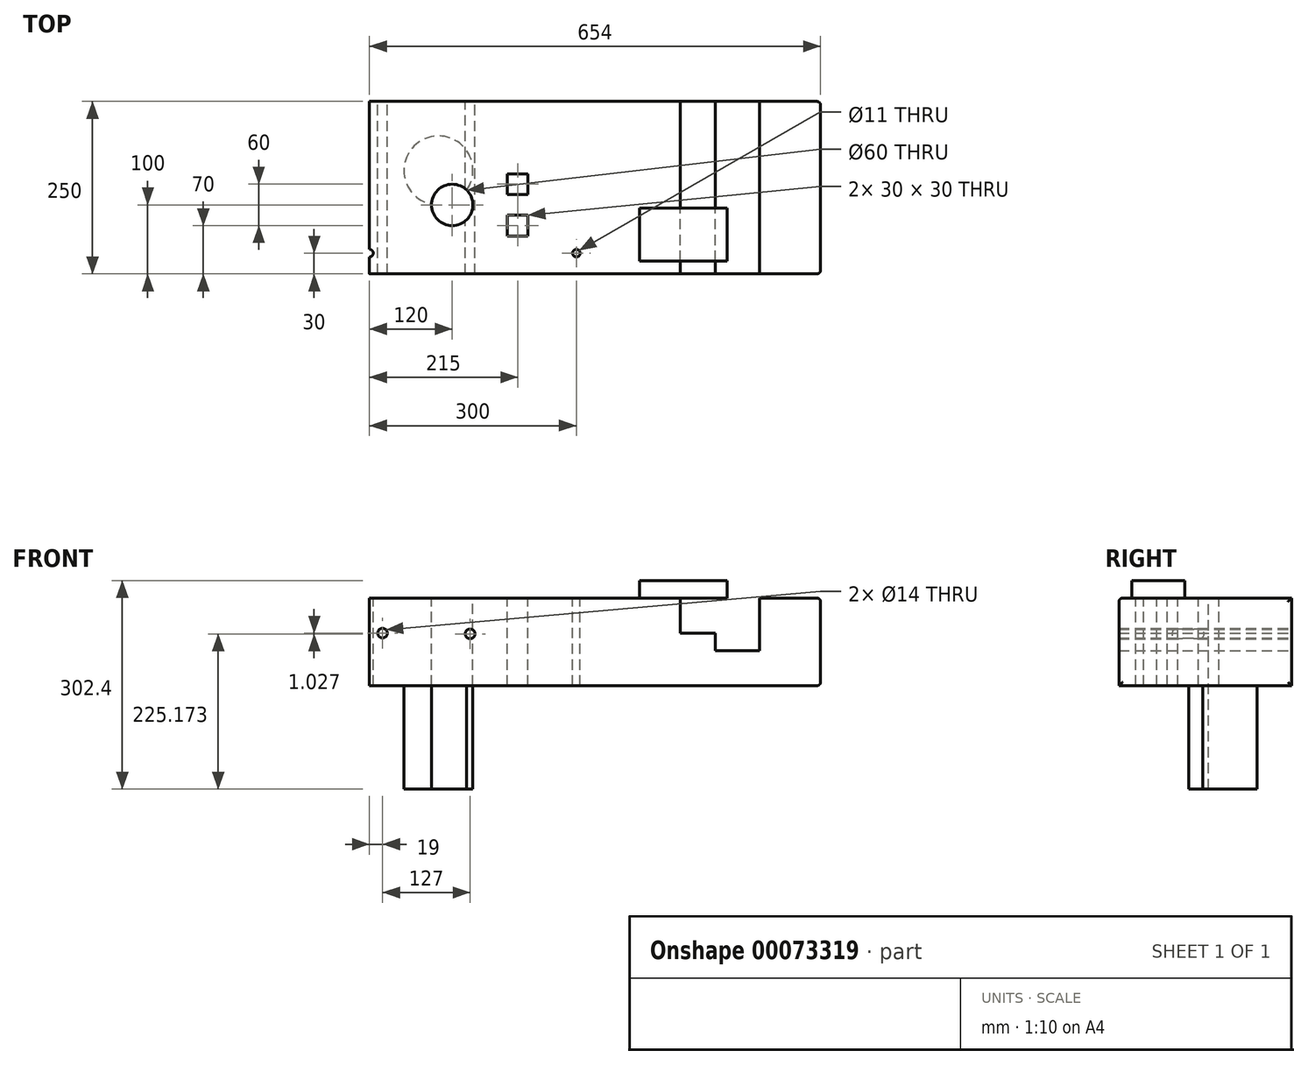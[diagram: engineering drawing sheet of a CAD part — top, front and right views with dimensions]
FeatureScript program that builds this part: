
annotation { "Feature Type Name" : "Feature", "Feature Type Description" : "" }
export const myFeature = defineFeature(function(context is Context, id is Id, definition is map)
    precondition{}
    {
        {
            var Q0;
            Q0=qCreatedBy(makeId("Top.planeOp"),FACE);
            var sketch = newSketch(context, id + "F0", { "sketchPlane" : qUnion([Q0])});
            skLineSegment(sketch, "E0.bottom", {"start": v(0, 0) * mm, "end": v(-400, 0) * mm});
            skLineSegment(sketch, "E0.top", {"start": v(0, -250) * mm, "end": v(-400, -250) * mm});
            skLineSegment(sketch, "E0.left", {"start": v(0, 0) * mm, "end": v(0, -250) * mm});
            skLineSegment(sketch, "E0.right", {"start": v(-400, 0) * mm, "end": v(-400, -250) * mm});
            skSolve(sketch);
        }
        {
            var Q0;
            Q0 = qSketchRegion(id + "F0", true);
            extrude(context, id + "F1", {"entities" : qUnion([Q0]), "depth" : 127 * mm});
        }
        {
            var Q0;
            Q0=makeQuery(id+"F1.opExtrude","CAP_FACE",FACE,{"disambiguationData":[OSD([sQuery(id+"F0.wireOp",EDGE,"E0.bottom"),sQuery(id+"F0.wireOp",EDGE,"E0.top"),sQuery(id+"F0.wireOp",EDGE,"E0.left"),sQuery(id+"F0.wireOp",EDGE,"E0.right")])],"isStart":true});
            var sketch = newSketch(context, id + "F2", { "sketchPlane" : qUnion([Q0])});
            skCircle(sketch, "E1", {"center": v(-300, 100) * mm, "radius": 50 * mm});
            skSolve(sketch);
        }
        {
            var Q0;
            Q0 = qSketchRegion(id + "F2", true);
            extrude(context, id + "F3", {"entities" : qUnion([Q0]), "operationType" : NewBodyOperationType.ADD, "offsetDistance" : 25 * mm, "depth" : 150 * mm});
        }
        {
            var Q0;
            Q0=makeQuery(id+"F0.imprint","IMPRINT",FACE,{"disambiguationData":[TD([[makeQuery(id+"F0.imprint","IMPRINT",EDGE,{"derivedFrom":sQuery(id+"F0.wireOp",EDGE,"E0.bottom")}),1.0]])]});
            var sketch = newSketch(context, id + "F4", { "sketchPlane" : qUnion([Q0])});
            skPoint(sketch, "E2", {"position": v(-400, -220) * mm});
            skPoint(sketch, "E3", {"position": v(-100, -220) * mm});
            skSolve(sketch);
        }
        {
            var Q0;
            Q0=sQuery(id+"F4.wireOp",VERTEX,"E2");
            var Q1;
            Q1=sQuery(id+"F4.wireOp",VERTEX,"E3");
            var Q2;
            Q2=makeQuery(id+"F1.opExtrude","SWEPT_BODY",BODY,{"disambiguationData":[OSD([sQuery(id+"F0.wireOp",EDGE,"E0.bottom"),sQuery(id+"F0.wireOp",EDGE,"E0.top"),sQuery(id+"F0.wireOp",EDGE,"E0.left"),sQuery(id+"F0.wireOp",EDGE,"E0.right")])]});
            hole(context, id + "F5", {"style" : HoleStyle.SIMPLE, "holeDiameter" : 11 * mm, "endStyle" : HoleEndStyle.THROUGH, "oppositeDirection" : true, "locations" : qUnion([Q0, Q1]), "scope" : qUnion([Q2]), "standardTappedOrClearance" : lookupTablePath({ "standard" : "ISO", "fit" : "Normal", "size" : "M10", "type" : "Clearance" }), "standardBlindInLast" : lookupTablePath({ "fit" : "Standard", "standard" : "ISO", "size" : "M10", "type" : "Clearance" }), "isTappedThrough" : true, "startStyle" : HoleStartStyle.PART});
        }
        {
            var Q0;
            Q0=makeQuery(id+"F1.opExtrude","SWEPT_FACE",FACE,{"disambiguationData":[OSD([sQuery(id+"F0.wireOp",EDGE,"E0.top")])]});
            var sketch = newSketch(context, id + "F6", { "sketchPlane" : qUnion([Q0])});
            skPoint(sketch, "E4", {"position": v(-381, 76.2) * mm});
            skPoint(sketch, "E5", {"position": v(-254, 75.17) * mm});
            skSolve(sketch);
        }
        {
            var Q0;
            Q0=sQuery(id+"F6.wireOp",VERTEX,"E4");
            var Q1;
            Q1=sQuery(id+"F6.wireOp",VERTEX,"E5");
            var Q2;
            Q2=makeQuery(id+"F1.opExtrude","SWEPT_BODY",BODY,{"disambiguationData":[OSD([sQuery(id+"F0.wireOp",EDGE,"E0.bottom"),sQuery(id+"F0.wireOp",EDGE,"E0.top"),sQuery(id+"F0.wireOp",EDGE,"E0.left"),sQuery(id+"F0.wireOp",EDGE,"E0.right")])]});
            hole(context, id + "F7", {"style" : HoleStyle.SIMPLE, "endStyle" : HoleEndStyle.THROUGH, "standardTappedOrClearance" : lookupTablePath({ "standard" : "ISO", "engagement" : "75%", "pitch" : "2 mm", "size" : "M16", "type" : "Tapped" }), "standardBlindInLast" : lookupTablePath({ "standard" : "ISO", "engagement" : "75%", "pitch" : "2 mm", "size" : "M16", "type" : "Tapped" }), "holeDiameter" : 14 * mm, "locations" : qUnion([Q0, Q1]), "scope" : qUnion([Q2]), "isTappedThrough" : true, "majorDiameter" : 16 * mm, "showTappedDepth" : true, "startStyle" : HoleStartStyle.PART});
        }
        {
            var Q0;
            Q0=makeQuery(id+"F1.opExtrude","SWEPT_FACE",FACE,{"disambiguationData":[OSD([sQuery(id+"F0.wireOp",EDGE,"E0.left")])]});
            extrude(context, id + "F8", {"entities" : qUnion([Q0]), "operationType" : NewBodyOperationType.ADD, "depth" : 254 * mm});
        }
        {
            var Q0;
            Q0=makeQuery(id+"F8.opExtrude","CAP_FACE",FACE,{"disambiguationData":[OSD([sQuery(id+"F0.wireOp",EDGE,"E0.left")])],"isStart":false});
            var Q1;
            {var subQ0=sQuery(id+"F0.wireOp",EDGE,"E0.right");var subQ1=sQuery(id+"F0.wireOp",EDGE,"E0.top");Q1=makeQuery(id+"FkXuBcG6GQTuiXg_1.opChamfer","BLEND_EDGE",EDGE,{"blendedFrom":[makeQuery(id+"F1.opExtrude","SWEPT_EDGE",EDGE,{"disambiguationData":[OSD([subQ1,subQ0])]}),makeQuery(id+"F1.opExtrude","CAP_FACE",FACE,{"disambiguationData":[OSD([sQuery(id+"F0.wireOp",EDGE,"E0.bottom"),subQ1,sQuery(id+"F0.wireOp",EDGE,"E0.left"),subQ0])],"isStart":false})],"blendedInto":[makeQuery(id+"F1.opExtrude","CAP_FACE",FACE,{"disambiguationData":[OSD([sQuery(id+"F0.wireOp",EDGE,"E0.bottom"),subQ1,sQuery(id+"F0.wireOp",EDGE,"E0.left"),subQ0])],"isStart":false})]});}
            var Q2;
            {var subQ0=sQuery(id+"F0.wireOp",EDGE,"E0.left");var subQ1=sQuery(id+"F0.wireOp",EDGE,"E0.top");Q2=makeQuery(id+"F8.boolean.opBoolean","MERGE",EDGE,{"derivedFrom":[makeQuery(id+"F1.opExtrude","CAP_EDGE",EDGE,{"disambiguationData":[OSD([subQ1])],"isStart":false}),makeQuery(id+"F8.opExtrude","SWEPT_EDGE",EDGE,{"disambiguationData":[OSD([subQ1,subQ0]),TDD([makeQuery(id+"F1.opExtrude","CAP_VERTEX",VERTEX,{"disambiguationData":[OSD([subQ1,subQ0])],"isStart":false})])]})]});}
            fillet(context, id + "F9", {"entities" : qUnion([Q0, Q1, Q2]), "radius" : 5.08 * mm, "tangentPropagation" : true, "allowEdgeOverflow" : false});
        }
        {
            var Q0;
            {var subQ0=sQuery(id+"F0.wireOp",EDGE,"E0.bottom");Q0=makeQuery(id+"F8.boolean.opBoolean","MERGE",FACE,{"derivedFrom":[makeQuery(id+"F1.opExtrude","SWEPT_FACE",FACE,{"disambiguationData":[OSD([subQ0])]}),makeQuery(id+"F8.opExtrude","SWEPT_FACE",FACE,{"disambiguationData":[OSD([subQ0,sQuery(id+"F0.wireOp",EDGE,"E0.left")])]})]});}
            var sketch = newSketch(context, id + "F10", { "sketchPlane" : qUnion([Q0])});
            skLineSegment(sketch, "E6", {"start": v(-165.62, 127) * mm, "end": v(-165.62, 50.8) * mm});
            skLineSegment(sketch, "E7", {"start": v(-165.62, 50.8) * mm, "end": v(-101.6, 50.8) * mm});
            skLineSegment(sketch, "E8", {"start": v(-101.6, 50.8) * mm, "end": v(-101.6, 76.2) * mm});
            skLineSegment(sketch, "E9", {"start": v(-101.6, 76.2) * mm, "end": v(-50.8, 76.2) * mm});
            skLineSegment(sketch, "E10", {"start": v(-50.8, 76.2) * mm, "end": v(-50.8, 127) * mm});
            skLineSegment(sketch, "E11", {"start": v(-50.8, 127) * mm, "end": v(-165.62, 127) * mm});
            skSolve(sketch);
        }
        {
            var Q0;
            Q0 = qSketchRegion(id + "F10", true);
            extrude(context, id + "F11", {"entities" : qUnion([Q0]), "operationType" : NewBodyOperationType.REMOVE, "endBound" : BoundingType.THROUGH_ALL, "oppositeDirection" : true, "depth" : 76.2 * mm});
        }
        {
            var Q0;
            {var subQ0=sQuery(id+"F0.wireOp",EDGE,"E0.left");Q0=makeQuery(id+"F11.boolean.opBoolean","MERGE",FACE,{"derivedFrom":[makeQuery(id+"F8.boolean.opBoolean","MERGE",FACE,{"derivedFrom":[makeQuery(id+"F1.opExtrude","CAP_FACE",FACE,{"disambiguationData":[OSD([sQuery(id+"F0.wireOp",EDGE,"E0.bottom"),sQuery(id+"F0.wireOp",EDGE,"E0.top"),subQ0,sQuery(id+"F0.wireOp",EDGE,"E0.right")])],"isStart":false}),makeQuery(id+"F8.opExtrude","SWEPT_FACE",FACE,{"disambiguationData":[OSD([subQ0]),TDD([makeQuery(id+"F1.opExtrude","CAP_EDGE",EDGE,{"disambiguationData":[OSD([subQ0])],"isStart":false})])]})]}),makeQuery(id+"F11.opExtrude","SWEPT_FACE",FACE,{"disambiguationData":[OSD([sQuery(id+"F10.wireOp",EDGE,"E11")])]})]});}
            var sketch = newSketch(context, id + "F12", { "sketchPlane" : qUnion([Q0])});
            skLineSegment(sketch, "E12.bottom", {"start": v(118.87, -154.91) * mm, "end": v(-8.13, -154.91) * mm});
            skLineSegment(sketch, "E12.top", {"start": v(118.87, -231.39) * mm, "end": v(-8.13, -231.39) * mm});
            skLineSegment(sketch, "E12.left", {"start": v(118.87, -154.91) * mm, "end": v(118.87, -231.39) * mm});
            skLineSegment(sketch, "E12.right", {"start": v(-8.13, -154.91) * mm, "end": v(-8.13, -231.39) * mm});
            skSolve(sketch);
        }
        {
            var Q0;
            Q0 = qSketchRegion(id + "F12", true);
            extrude(context, id + "F13", {"entities" : qUnion([Q0]), "operationType" : NewBodyOperationType.ADD, "depth" : 25.4 * mm});
        }
        {
            var Q0;
            {var subQ0=sQuery(id+"F0.wireOp",EDGE,"E0.left");Q0=makeQuery(id+"F11.boolean.opBoolean","MERGE",FACE,{"derivedFrom":[makeQuery(id+"F8.boolean.opBoolean","MERGE",FACE,{"derivedFrom":[makeQuery(id+"F1.opExtrude","CAP_FACE",FACE,{"disambiguationData":[OSD([sQuery(id+"F0.wireOp",EDGE,"E0.bottom"),sQuery(id+"F0.wireOp",EDGE,"E0.top"),subQ0,sQuery(id+"F0.wireOp",EDGE,"E0.right")])],"isStart":false}),makeQuery(id+"F8.opExtrude","SWEPT_FACE",FACE,{"disambiguationData":[OSD([subQ0]),TDD([makeQuery(id+"F1.opExtrude","CAP_EDGE",EDGE,{"disambiguationData":[OSD([subQ0])],"isStart":false})])]})]}),makeQuery(id+"F11.opExtrude","SWEPT_FACE",FACE,{"disambiguationData":[OSD([sQuery(id+"F10.wireOp",EDGE,"E11")])]})]});}
            var sketch = newSketch(context, id + "F14", { "sketchPlane" : qUnion([Q0])});
            skLineSegment(sketch, "E13.bottom", {"start": v(-170, -105) * mm, "end": v(-200, -105) * mm});
            skLineSegment(sketch, "E13.top", {"start": v(-170, -135) * mm, "end": v(-200, -135) * mm});
            skLineSegment(sketch, "E13.left", {"start": v(-170, -105) * mm, "end": v(-170, -135) * mm});
            skLineSegment(sketch, "E13.right", {"start": v(-200, -105) * mm, "end": v(-200, -135) * mm});
            skLineSegment(sketch, "E14.bottom", {"start": v(-200, -165) * mm, "end": v(-170, -165) * mm});
            skLineSegment(sketch, "E14.top", {"start": v(-200, -195) * mm, "end": v(-170, -195) * mm});
            skLineSegment(sketch, "E14.left", {"start": v(-200, -165) * mm, "end": v(-200, -195) * mm});
            skLineSegment(sketch, "E14.right", {"start": v(-170, -165) * mm, "end": v(-170, -195) * mm});
            skCircle(sketch, "E15", {"center": v(-280, -150) * mm, "radius": 30 * mm});
            skLineSegment(sketch, "E16", {"start": v(-280, -150) * mm, "end": v(-117.29, -150) * mm, "construction": true});
            skSolve(sketch);
        }
        {
            var Q0;
            Q0 = qSketchRegion(id + "F14", true);
            extrude(context, id + "F15", {"entities" : qUnion([Q0]), "operationType" : NewBodyOperationType.REMOVE, "endBound" : BoundingType.THROUGH_ALL, "oppositeDirection" : true, "depth" : 25.4 * mm});
        }
    });
